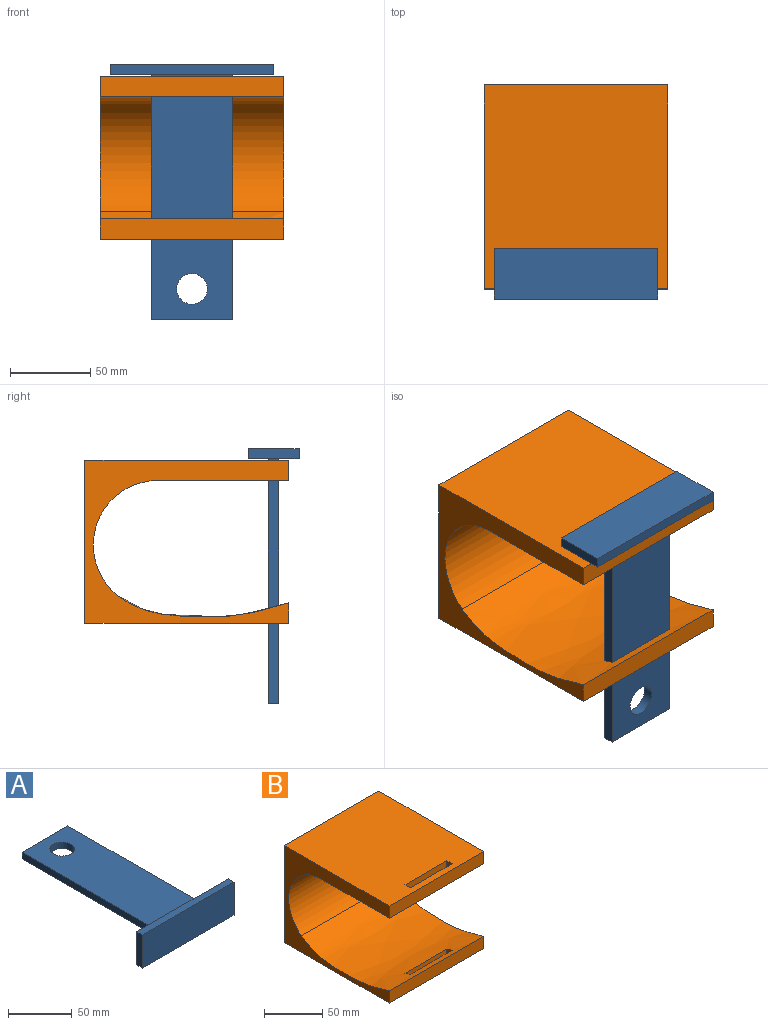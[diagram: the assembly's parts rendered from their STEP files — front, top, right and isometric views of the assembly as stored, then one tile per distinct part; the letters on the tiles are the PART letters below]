
ASSEMBLY  parts=2 mates=1
PART A: 12 faces, bbox 101.6x158.8x31.8 mm
  f0: plane 152.4x50.8mm, normal (0,0,-1), area 7456.9mm2, adj f1,f3,f4,f5,f11
  f1: plane 50.8x6.35mm, normal (0,1,0), area 322.6mm2, adj f0,f2,f3,f4
  f2: plane 152.4x50.8mm, normal (0,0,1), area 7456.9mm2, adj f1,f3,f4,f5,f11
  f3: plane 152.4x6.35mm, normal (1,0,0), area 967.7mm2, adj f0,f1,f2,f5
  f4: plane 152.4x6.35mm, normal (-1,0,0), area 967.7mm2, adj f0,f1,f2,f5
  f5: plane 101.6x31.75mm, normal (0,1,0), area 2903.2mm2, adj f0,f2,f3,f4,f6,f7,f9,f10
  f6: plane 101.6x6.35mm, normal (0,0,-1), area 645.2mm2, adj f5,f8,f9,f10
  f7: plane 101.6x6.35mm, normal (0,0,1), area 645.2mm2, adj f5,f8,f9,f10
  f8: plane 101.6x31.75mm, normal (0,-1,0), area 3225.8mm2, adj f6,f7,f9,f10
  f9: plane 31.75x6.35mm, normal (1,0,0), area 201.6mm2, adj f5,f6,f7,f8
  f10: plane 31.75x6.35mm, normal (-1,0,0), area 201.6mm2, adj f5,f6,f7,f8
  f11: cylinder r=9.53mm len=19.05mm, axis (0,0,-1), area 380mm2, adj f0,f2
PART B: 18 faces, bbox 114.3x127x101.6 mm
  f0: plane 127x114.3mm, normal (0,0,-1), area 14193.4mm2, adj f5,f6,f7,f8,f10,f11,f12,f13
  f1: plane 127x114.3mm, normal (0,0,1), area 14193.4mm2, adj f4,f5,f6,f8,f14,f15,f16,f17
  f2: plane 114.3x81.59mm, normal (0,0,-1), area 9003.4mm2, adj f4,f5,f6,f9,f14,f15,f16,f17
  f3: extruded ~114.3x106.56mm, area 12270.2mm2, adj f5,f6,f7,f9,f10,f11,f12,f13
  f4: plane 114.3x12.7mm, normal (0,-1,0), area 1451.6mm2, adj f1,f2,f5,f6
  f5: plane 127x101.6mm, normal (-1,0,0), area 3582.7mm2, adj f0,f1,f2,f3,f4,f7,f8,f9
  f6: plane 127x101.6mm, normal (1,0,0), area 3582.7mm2, adj f0,f1,f2,f3,f4,f7,f8,f9
  f7: plane 114.3x12.7mm, normal (0,-1,0), area 1451.6mm2, adj f0,f3,f5,f6
  f8: plane 114.3x101.6mm, normal (0,1,0), area 11612.9mm2, adj f0,f1,f5,f6
  f9: cylinder r=40.18mm len=114.3mm, axis (1,0,0), area 11349.5mm2, adj f2,f3,f5,f6
  f10: plane 10.71x6.38mm, normal (1,0,0), area 62.1mm2, adj f0,f3,f11,f13
  f11: plane 50.8x8.91mm, normal (0,-1,0), area 452.4mm2, adj f0,f3,f10,f12
  f12: plane 10.71x6.38mm, normal (-1,0,0), area 62.1mm2, adj f0,f3,f11,f13
  f13: plane 50.8x10.7mm, normal (0,1,0), area 543.3mm2, adj f0,f3,f10,f12
  f14: plane 50.8x12.7mm, normal (0,1,0), area 645.2mm2, adj f1,f2,f15,f17
  f15: plane 12.7x6.35mm, normal (-1,0,0), area 80.7mm2, adj f1,f2,f14,f16
  f16: plane 50.8x12.7mm, normal (0,-1,0), area 645.2mm2, adj f1,f2,f15,f17
  f17: plane 12.7x6.35mm, normal (1,0,0), area 80.7mm2, adj f1,f2,f14,f16
PLACE A rot(axis=(-1,0,0),90deg) t=(-326.95,146.64,-158)mm
PLACE B t=(-319.26,273.4,-159.03)mm
MATE slider A.f5 <-> B.f1  axis (0,0,-1) through (-276.15,159.1,-94.78)mm
